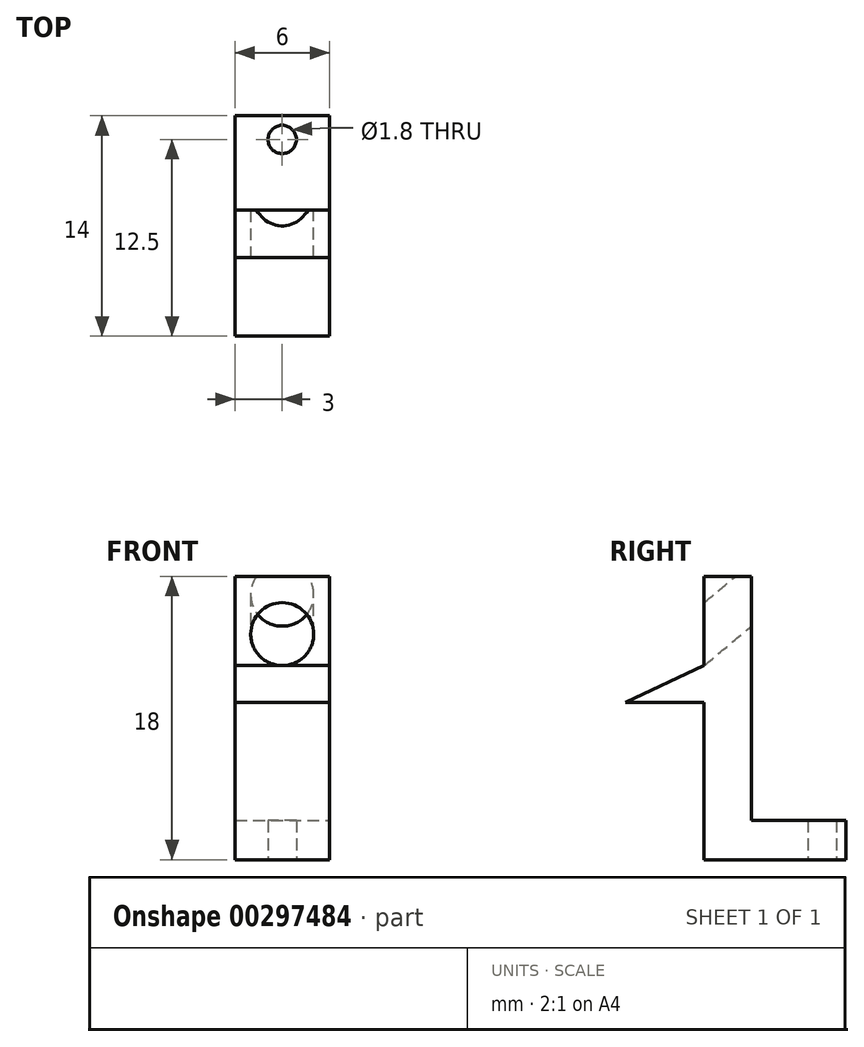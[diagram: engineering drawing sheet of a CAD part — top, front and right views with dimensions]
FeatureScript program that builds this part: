
annotation { "Feature Type Name" : "Feature", "Feature Type Description" : "" }
export const myFeature = defineFeature(function(context is Context, id is Id, definition is map)
    precondition{}
    {
        {
            var Q0;
            Q0=qCreatedBy(makeId("Right.planeOp"),FACE);
            var sketch = newSketch(context, id + "F0", { "sketchPlane" : qUnion([Q0])});
            skLineSegment(sketch, "E0", {"start": v(0, 0) * mm, "end": v(-3, 0) * mm});
            skLineSegment(sketch, "E1", {"start": v(-3, 0) * mm, "end": v(-3, 10) * mm});
            skLineSegment(sketch, "E2", {"start": v(-3, 10) * mm, "end": v(-8, 10) * mm});
            skLineSegment(sketch, "E3", {"start": v(-8, 10) * mm, "end": v(-3, 12.33) * mm});
            skLineSegment(sketch, "E4", {"start": v(0, 13.73) * mm, "end": v(0, 2.5) * mm});
            skLineSegment(sketch, "E5", {"start": v(0, 0) * mm, "end": v(6, 0) * mm});
            skLineSegment(sketch, "E6", {"start": v(6, 0) * mm, "end": v(6, 2.5) * mm});
            skLineSegment(sketch, "E7", {"start": v(6, 2.5) * mm, "end": v(0, 2.5) * mm});
            skLineSegment(sketch, "E8", {"start": v(0, 13.73) * mm, "end": v(0, 18) * mm});
            skLineSegment(sketch, "E9", {"start": v(0, 18) * mm, "end": v(-3, 18) * mm});
            skLineSegment(sketch, "E10", {"start": v(-3, 18) * mm, "end": v(-3, 12.33) * mm});
            skSolve(sketch);
        }
        {
            var Q0;
            Q0=makeQuery(id+"F0.imprint","IMPRINT",FACE,{"disambiguationData":[TD([[makeQuery(id+"F0.imprint","IMPRINT",EDGE,{"derivedFrom":sQuery(id+"F0.wireOp",EDGE,"E0")}),-1.0]])]});
            extrude(context, id + "F1", {"entities" : qUnion([Q0]), "oppositeDirection" : true, "depth" : 6 * mm});
        }
        {
            var Q0;
            Q0=qCreatedBy(makeId("Top.planeOp"),FACE);
            var sketch = newSketch(context, id + "F2", { "sketchPlane" : qUnion([Q0])});
            skPoint(sketch, "E11", {"position": v(-3, 4.5) * mm});
            skSolve(sketch);
        }
        {
            var Q0;
            Q0=sQuery(id+"F2.wireOp",VERTEX,"E11");
            var Q1;
            Q1=makeQuery(id+"F1.opExtrude","SWEPT_BODY",BODY,{"disambiguationData":[OSD([sQuery(id+"F0.wireOp",EDGE,"E0"),sQuery(id+"F0.wireOp",EDGE,"E1"),sQuery(id+"F0.wireOp",EDGE,"E2"),sQuery(id+"F0.wireOp",EDGE,"E3"),sQuery(id+"F0.wireOp",EDGE,"E4"),sQuery(id+"F0.wireOp",EDGE,"E5"),sQuery(id+"F0.wireOp",EDGE,"E6"),sQuery(id+"F0.wireOp",EDGE,"E7")])]});
            hole(context, id + "F3", {"style" : HoleStyle.SIMPLE, "endStyle" : HoleEndStyle.THROUGH, "oppositeDirection" : true, "holeDiameter" : 1.8 * mm, "tappedDepth" : 12 * mm, "tapClearance" : 3, "locations" : qUnion([Q0]), "scope" : qUnion([Q1])});
        }
        {
            var Q0;
            Q0=qCreatedBy(makeId("Front.planeOp"),FACE);
            var sketch = newSketch(context, id + "F4", { "sketchPlane" : qUnion([Q0])});
            skCircle(sketch, "E12", {"center": v(-3, 16.83) * mm, "radius": 2 * mm});
            skSolve(sketch);
        }
        {
            var Q0;
            Q0=makeQuery(id+"F1.opExtrude","SWEPT_FACE",FACE,{"disambiguationData":[OSD([sQuery(id+"F0.wireOp",EDGE,"E10")])]});
            var sketch = newSketch(context, id + "F5", { "sketchPlane" : qUnion([Q0])});
            skCircle(sketch, "E13", {"center": v(-3, 14.33) * mm, "radius": 2 * mm});
            skSolve(sketch);
        }
        {
            var Q0;
            Q0=qCreatedBy(makeId("Right.planeOp"),FACE);
            var sketch = newSketch(context, id + "F6", { "sketchPlane" : qUnion([Q0])});
            skLineSegment(sketch, "E14", {"start": v(-3, 14.33) * mm, "end": v(0, 16.83) * mm});
            skSolve(sketch);
        }
        {
            var Q0;
            Q0=makeQuery(id+"F5.imprint","IMPRINT",FACE,{"disambiguationData":[TD([[makeQuery(id+"F5.imprint","IMPRINT",EDGE,{"derivedFrom":sQuery(id+"F5.wireOp",EDGE,"E13")}),1.0]])]});
            var Q1;
            Q1=sQuery(id+"F6.wireOp",EDGE,"E14");
            sweep(context, id + "F7", {"operationType" : NewBodyOperationType.REMOVE, "profiles" : qUnion([Q0]), "path" : qUnion([Q1])});
        }
    });
